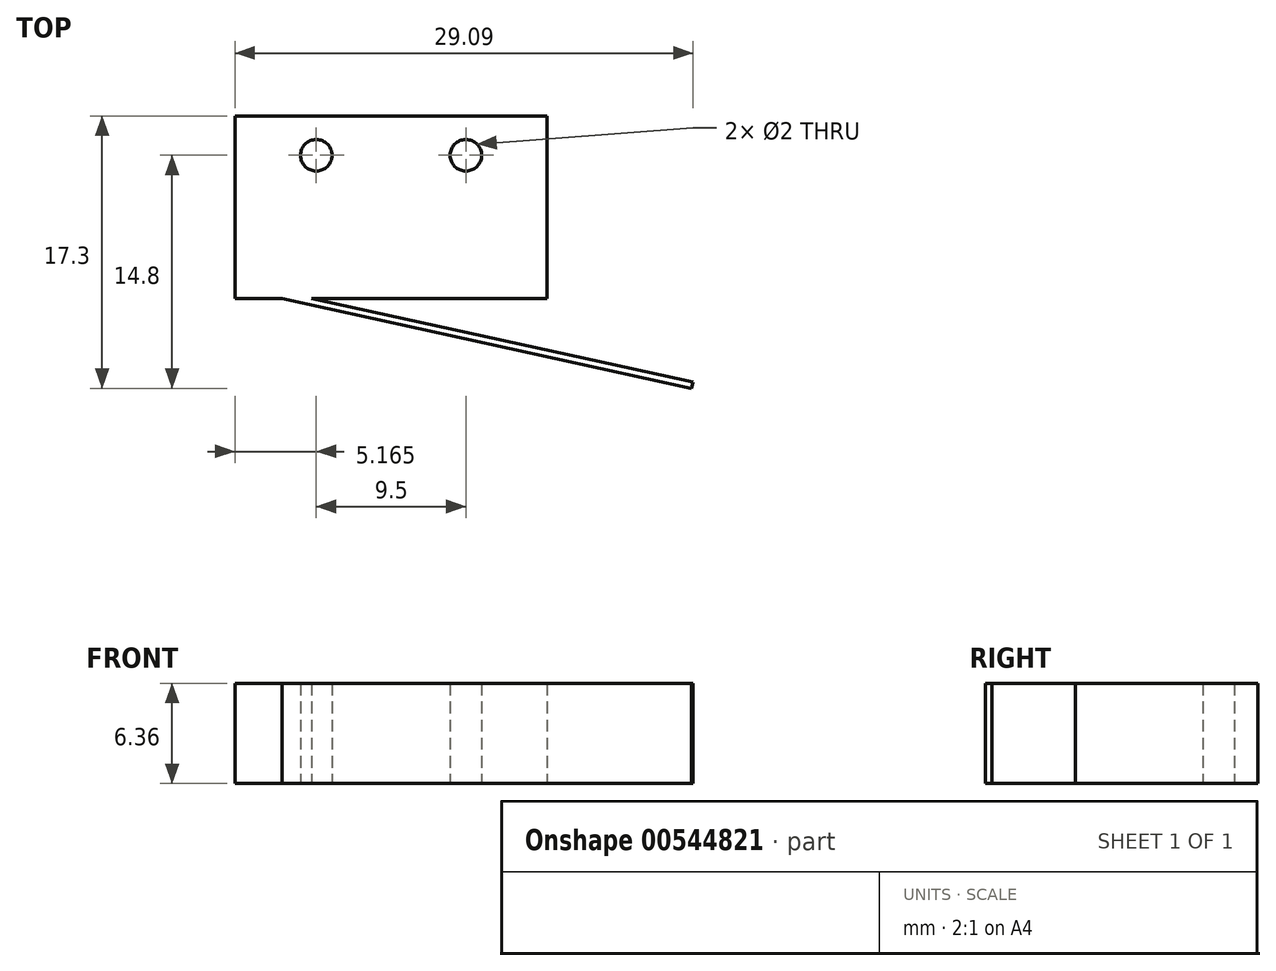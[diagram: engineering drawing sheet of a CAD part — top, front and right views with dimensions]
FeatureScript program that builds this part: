
annotation { "Feature Type Name" : "Feature", "Feature Type Description" : "" }
export const myFeature = defineFeature(function(context is Context, id is Id, definition is map)
    precondition{}
    {
        {
            var Q0;
            Q0=qCreatedBy(makeId("Top.planeOp"),FACE);
            var sketch = newSketch(context, id + "F0", { "sketchPlane" : qUnion([Q0])});
            skLineSegment(sketch, "E0.right", {"start": v(19.83, 0) * mm, "end": v(19.83, 11.6) * mm});
            skLineSegment(sketch, "E1.MirrorCS", {"start": v(48.92, -5.3) * mm, "end": v(48.83, -5.7) * mm});
            skLineSegment(sketch, "E2.MirrorCS", {"start": v(34.5, 7.92) * mm, "end": v(34.5, 10.28) * mm, "construction": true});
            skLineSegment(sketch, "E3.MirrorCS", {"start": v(25, 7.92) * mm, "end": v(25, 10.28) * mm, "construction": true});
            skLineSegment(sketch, "E4.MirrorCS", {"start": v(22.83, 0) * mm, "end": v(19.83, 0) * mm});
            skLineSegment(sketch, "E5.MirrorCS", {"start": v(39.66, 11.6) * mm, "end": v(19.83, 11.6) * mm});
            skCircle(sketch, "E6.MirrorC", {"center": v(34.5, 9.1) * mm, "radius": 1 * mm});
            skLineSegment(sketch, "E7.MirrorCS", {"start": v(24.7, 0) * mm, "end": v(48.92, -5.3) * mm});
            skLineSegment(sketch, "E8.MirrorCS", {"start": v(19.83, 0) * mm, "end": v(22.83, 0) * mm, "construction": true});
            skLineSegment(sketch, "E9.MirrorCS", {"start": v(25, 10.28) * mm, "end": v(34.5, 10.28) * mm, "construction": true});
            skCircle(sketch, "E10.MirrorC", {"center": v(25, 9.1) * mm, "radius": 1 * mm});
            skLineSegment(sketch, "E11.MirrorCS", {"start": v(22.83, 0) * mm, "end": v(48.83, -5.7) * mm});
            skLineSegment(sketch, "E12.MirrorCS", {"start": v(25, 7.92) * mm, "end": v(34.5, 7.92) * mm, "construction": true});
            skLineSegment(sketch, "E13.MirrorCS", {"start": v(39.66, 9.1) * mm, "end": v(19.83, 9.1) * mm, "construction": true});
            skLineSegment(sketch, "E14.MirrorCS", {"start": v(39.66, 11.6) * mm, "end": v(39.66, 9.1) * mm, "construction": true});
            skLineSegment(sketch, "E15.MirrorCS", {"start": v(39.66, 0) * mm, "end": v(24.7, 0) * mm});
            skPoint(sketch, "E16.MirrorP", {"position": v(29.74, 9.1) * mm});
            skLineSegment(sketch, "E17.MirrorCS", {"start": v(39.66, 0) * mm, "end": v(39.66, 11.6) * mm});
            skSolve(sketch);
        }
        {
            var Q0;
            Q0 = qSketchRegion(id + "F0", true);
            extrude(context, id + "F1", {"entities" : qUnion([Q0]), "depth" : 6.36 * mm, "offsetDistance" : 25 * mm});
        }
    });
